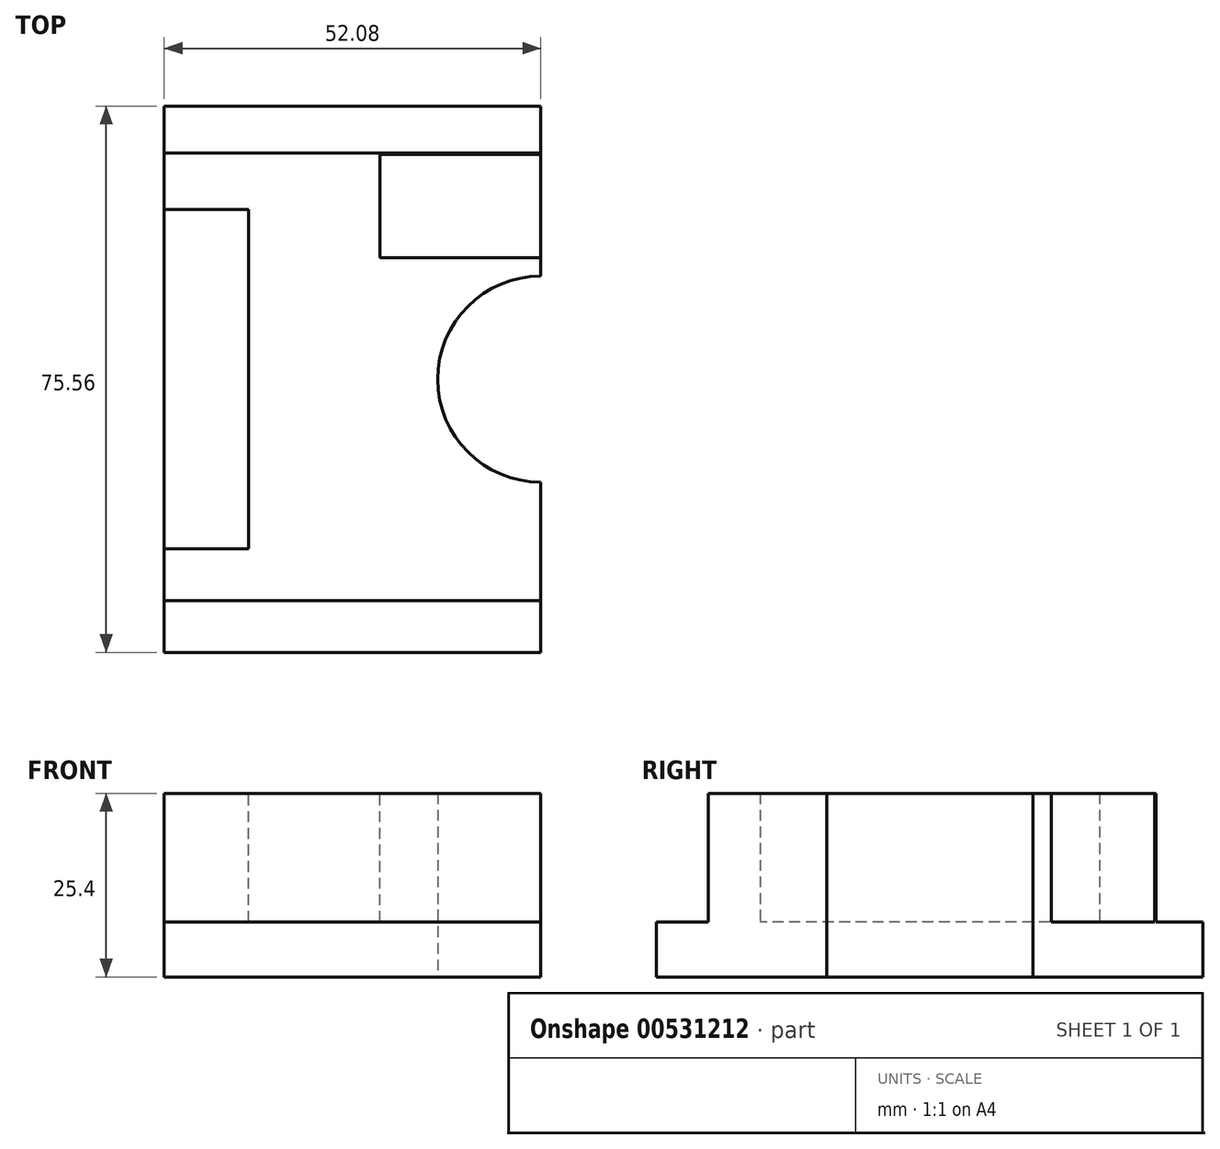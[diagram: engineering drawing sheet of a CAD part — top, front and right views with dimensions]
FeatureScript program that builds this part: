
annotation { "Feature Type Name" : "Feature", "Feature Type Description" : "" }
export const myFeature = defineFeature(function(context is Context, id is Id, definition is map)
    precondition{}
    {
        {
            var Q0;
            Q0=qCreatedBy(makeId("Top.planeOp"),FACE);
            var sketch = newSketch(context, id + "F0", { "sketchPlane" : qUnion([Q0])});
            skLineSegment(sketch, "E0.bottom", {"start": v(-26.04, 37.78) * mm, "end": v(26.04, 37.78) * mm});
            skLineSegment(sketch, "E0.top", {"start": v(-26.04, -37.78) * mm, "end": v(26.04, -37.78) * mm});
            skLineSegment(sketch, "E0.left", {"start": v(-26.04, 37.78) * mm, "end": v(-26.04, -37.78) * mm});
            skLineSegment(sketch, "E0.right", {"start": v(26.04, 37.78) * mm, "end": v(26.04, -37.78) * mm});
            skPoint(sketch, "E0.middle", {"position": v(0, 0) * mm});
            skCircle(sketch, "E1", {"center": v(26.04, 0) * mm, "radius": 14.25 * mm});
            skSolve(sketch);
        }
        {
            var Q0;
            Q0=makeQuery(id+"F0.imprint","IMPRINT",FACE,{"disambiguationData":[TD([[makeQuery(id+"F0.imprint","IMPRINT",EDGE,{"derivedFrom":sQuery(id+"F0.wireOp",EDGE,"E0.bottom")}),-1.0]])]});
            extrude(context, id + "F1", {"entities" : qUnion([Q0]), "depth" : 25.4 * mm, "offsetDistance" : 25.4 * mm});
        }
        {
            var Q0;
            Q0=makeQuery(id+"F1.opExtrude","CAP_FACE",FACE,{"disambiguationData":[OSD([sQuery(id+"F0.wireOp",EDGE,"E0.bottom"),sQuery(id+"F0.wireOp",EDGE,"E0.top"),sQuery(id+"F0.wireOp",EDGE,"E0.left"),sQuery(id+"F0.wireOp",EDGE,"E0.right"),sQuery(id+"F0.wireOp",EDGE,"E1")])],"isStart":false});
            var sketch = newSketch(context, id + "F2", { "sketchPlane" : qUnion([Q0])});
            skLineSegment(sketch, "E2.bottom", {"start": v(-37.7, 23.48) * mm, "end": v(-14.36, 23.48) * mm});
            skLineSegment(sketch, "E2.top", {"start": v(-37.7, -23.48) * mm, "end": v(-14.36, -23.48) * mm});
            skLineSegment(sketch, "E2.left", {"start": v(-37.7, 23.48) * mm, "end": v(-37.7, -23.48) * mm});
            skLineSegment(sketch, "E2.right", {"start": v(-14.36, 23.48) * mm, "end": v(-14.36, -23.48) * mm});
            skPoint(sketch, "E2.middle", {"position": v(-26.04, 0) * mm});
            skSolve(sketch);
        }
        {
            var Q0;
            Q0 = qSketchRegion(id + "F2", true);
            extrude(context, id + "F3", {"entities" : qUnion([Q0]), "operationType" : NewBodyOperationType.REMOVE, "oppositeDirection" : true, "depth" : 17.78 * mm, "offsetDistance" : 25.4 * mm});
        }
        {
            var Q0;
            Q0=makeQuery(id+"F1.opExtrude","CAP_FACE",FACE,{"disambiguationData":[OSD([sQuery(id+"F0.wireOp",EDGE,"E0.bottom"),sQuery(id+"F0.wireOp",EDGE,"E0.top"),sQuery(id+"F0.wireOp",EDGE,"E0.left"),sQuery(id+"F0.wireOp",EDGE,"E0.right"),sQuery(id+"F0.wireOp",EDGE,"E1")])],"isStart":false});
            var sketch = newSketch(context, id + "F4", { "sketchPlane" : qUnion([Q0])});
            skLineSegment(sketch, "E3.bottom", {"start": v(-26.04, -30.63) * mm, "end": v(26.04, -30.63) * mm});
            skLineSegment(sketch, "E3.left", {"start": v(-26.04, -30.63) * mm, "end": v(-26.04, -44.93) * mm});
            skLineSegment(sketch, "E3.right", {"start": v(26.04, -30.63) * mm, "end": v(26.04, -44.93) * mm});
            skPoint(sketch, "E3.middle", {"position": v(0, -37.78) * mm});
            skPoint(sketch, "E4.1.0.0", {"position": v(25.4, -37.78) * mm});
            skPoint(sketch, "E4.2.0.0", {"position": v(50.8, -37.78) * mm});
            skLineSegment(sketch, "E4.direction1", {"start": v(0, -37.78) * mm, "end": v(25.4, -37.78) * mm, "construction": true});
            skLineSegment(sketch, "E5.0.1.1", {"start": v(-26.04, 45.57) * mm, "end": v(-26.04, 31.27) * mm});
            skLineSegment(sketch, "E5.0.1.2", {"start": v(-26.04, 31.27) * mm, "end": v(26.04, 31.27) * mm});
            skLineSegment(sketch, "E5.0.1.3", {"start": v(26.04, 45.57) * mm, "end": v(26.04, 31.27) * mm});
            skLineSegment(sketch, "E5.1.0.1", {"start": v(-0.64, -30.63) * mm, "end": v(-0.64, -44.93) * mm});
            skLineSegment(sketch, "E5.1.1.1", {"start": v(-0.64, 45.57) * mm, "end": v(-0.64, 31.27) * mm});
            skLineSegment(sketch, "E5.direction1", {"start": v(-26.04, -30.63) * mm, "end": v(-0.64, -30.63) * mm, "construction": true});
            skLineSegment(sketch, "E5.direction2", {"start": v(-26.04, -30.63) * mm, "end": v(-26.04, 45.57) * mm, "construction": true});
            skLineSegment(sketch, "E6", {"start": v(26.04, 45.57) * mm, "end": v(-0.64, 45.57) * mm});
            skLineSegment(sketch, "E7", {"start": v(-0.64, 45.57) * mm, "end": v(-26.04, 45.57) * mm});
            skSolve(sketch);
        }
        {
            var Q0;
            {var subQ0=sQuery(id+"F4.wireOp",EDGE,"E3.bottom");Q0=makeQuery(id+"F4.imprint","IMPRINT",FACE,{"disambiguationData":[TD([[makeQuery(id+"F4.imprint","IMPRINT",EDGE,{"derivedFrom":subQ0}),-1.0]])]});}
            extrude(context, id + "F5", {"entities" : qUnion([Q0]), "operationType" : NewBodyOperationType.REMOVE, "oppositeDirection" : true, "depth" : 17.78 * mm, "offsetDistance" : 25.4 * mm});
        }
        {
            var Q0;
            {var subQ1=sQuery(id+"F4.wireOp",EDGE,"E5.0.1.2");var subQ5=sQuery(id+"F4.wireOp",EDGE,"E5.1.1.1");var subQ6=makeQuery(id+"F4.imprint","INTERSECT",VERTEX,{"derivedFrom":[subQ1,subQ5]});Q0=makeQuery(id+"F4.imprint","IMPRINT",FACE,{"disambiguationData":[TD([[makeQuery(id+"F4.imprint","IMPRINT",EDGE,{"disambiguationData":[TD([[subQ6,1.0]])],"derivedFrom":subQ5}),1.0]])]});}
            var Q1;
            {var subQ4=sQuery(id+"F4.wireOp",EDGE,"E5.0.1.2");var subQ7=sQuery(id+"F4.wireOp",EDGE,"E5.1.1.1");var subQ8=makeQuery(id+"F4.imprint","INTERSECT",VERTEX,{"derivedFrom":[subQ4,subQ7]});Q1=makeQuery(id+"F4.imprint","IMPRINT",FACE,{"disambiguationData":[TD([[makeQuery(id+"F4.imprint","IMPRINT",EDGE,{"disambiguationData":[TD([[subQ8,1.0]])],"derivedFrom":subQ7}),-1.0]])]});}
            extrude(context, id + "F6", {"entities" : qUnion([Q0, Q1]), "operationType" : NewBodyOperationType.REMOVE, "oppositeDirection" : true, "depth" : 17.78 * mm, "offsetDistance" : 25.4 * mm});
        }
        {
            var Q0;
            {var subQ2=sQuery(id+"F0.wireOp",EDGE,"E1");var subQ3=makeQuery(id+"F1.opExtrude","CAP_EDGE",EDGE,{"disambiguationData":[OSD([subQ2])],"isStart":false});Q0=makeQuery(id+"F4.imprint","IMPRINT",FACE,{"disambiguationData":[TD([[makeQuery(id+"F4.imprint","IMPRINT",EDGE,{"derivedFrom":subQ3}),-1.0]])]});}
            var sketch = newSketch(context, id + "F7", { "sketchPlane" : qUnion([Q0])});
            skLineSegment(sketch, "E8.bottom", {"start": v(26.67, 16.83) * mm, "end": v(3.81, 16.83) * mm});
            skLineSegment(sketch, "E8.top", {"start": v(26.67, 31.12) * mm, "end": v(3.81, 31.12) * mm});
            skLineSegment(sketch, "E8.left", {"start": v(26.67, 16.83) * mm, "end": v(26.67, 31.12) * mm});
            skLineSegment(sketch, "E8.right", {"start": v(3.81, 16.83) * mm, "end": v(3.81, 31.12) * mm});
            skSolve(sketch);
        }
        {
            var Q0;
            {var subQ0=sQuery(id+"F7.wireOp",EDGE,"E8.right");Q0=makeQuery(id+"F7.imprint","IMPRINT",FACE,{"disambiguationData":[TD([[makeQuery(id+"F7.imprint","IMPRINT",EDGE,{"derivedFrom":subQ0}),-1.0]])]});}
            extrude(context, id + "F8", {"entities" : qUnion([Q0]), "operationType" : NewBodyOperationType.REMOVE, "oppositeDirection" : true, "depth" : 17.78 * mm, "offsetDistance" : 25.4 * mm});
        }
    });
